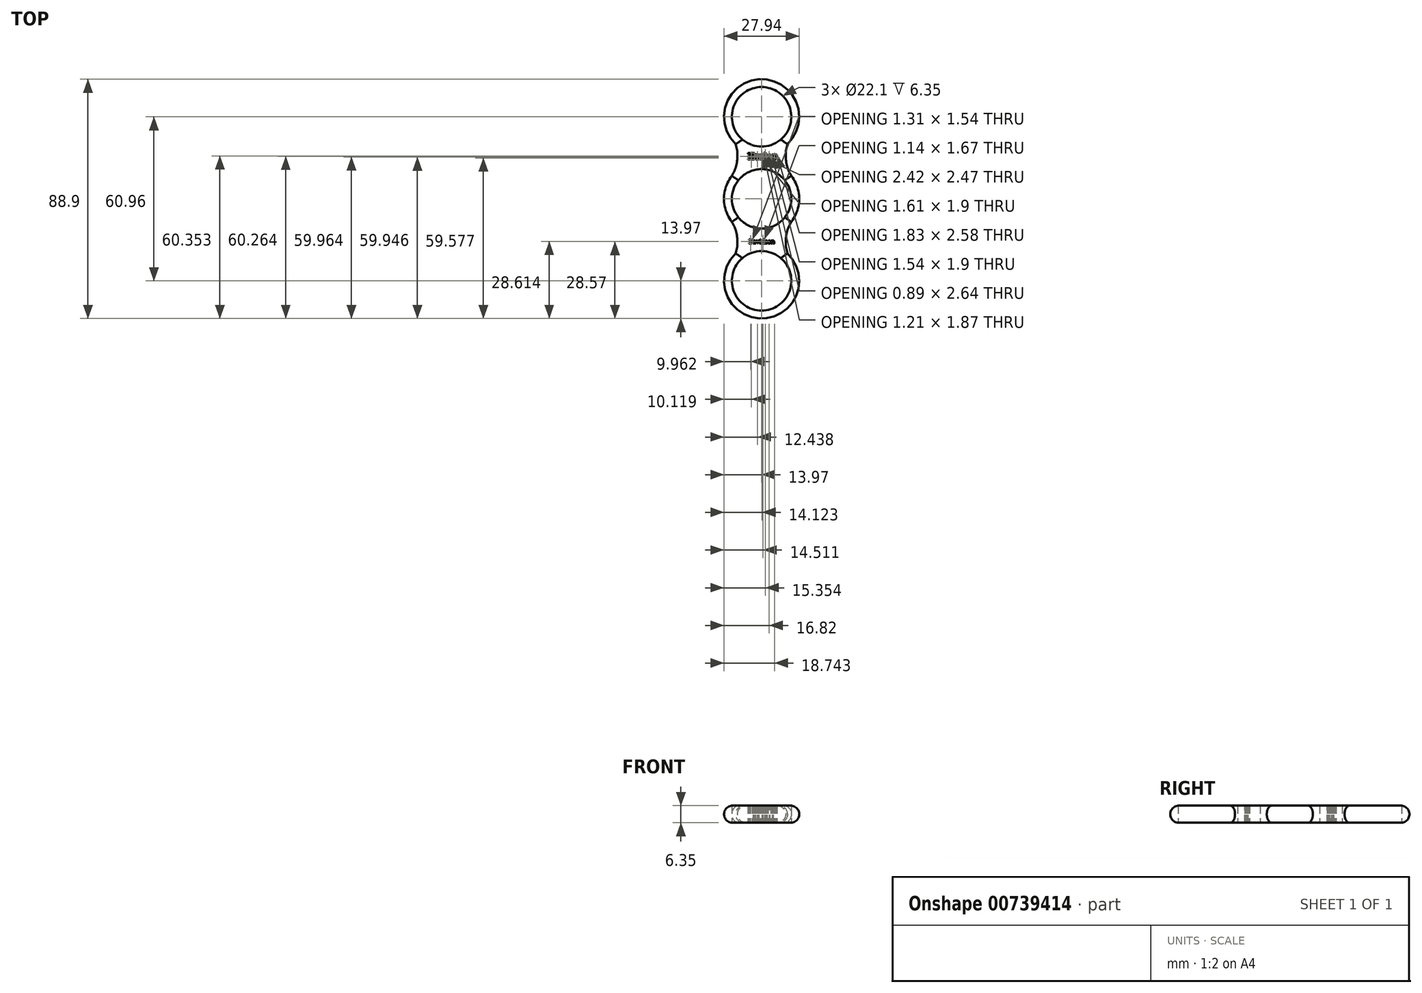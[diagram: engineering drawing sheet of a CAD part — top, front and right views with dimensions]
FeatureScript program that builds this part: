
annotation { "Feature Type Name" : "Feature", "Feature Type Description" : "" }
export const myFeature = defineFeature(function(context is Context, id is Id, definition is map)
    precondition{}
    {
        {
            var Q0;
            Q0=qCreatedBy(makeId("Top.planeOp"),FACE);
            var sketch = newSketch(context, id + "F0", { "sketchPlane" : qUnion([Q0])});
            skCircle(sketch, "E0", {"center": v(0, 0) * mm, "radius": 11.05 * mm});
            skArc(sketch, "E1", {"start": v(-11.04, 8.56) * mm, "mid": v(-13.97, 0) * mm, "end": v(-11.04, -8.56) * mm});
            skLineSegment(sketch, "E2", {"start": v(0, 0) * mm, "end": v(0, 30.48) * mm});
            skCircle(sketch, "E3", {"center": v(0, 30.48) * mm, "radius": 11.05 * mm});
            skArc(sketch, "E4", {"start": v(9.62, 20.35) * mm, "mid": v(0, 44.45) * mm, "end": v(-9.62, 20.35) * mm});
            skArc(sketch, "E5.MirrorC", {"start": v(9.62, -20.35) * mm, "mid": v(0, -44.45) * mm, "end": v(-9.62, -20.35) * mm});
            skCircle(sketch, "E6.MirrorC", {"center": v(0, -30.48) * mm, "radius": 11.05 * mm});
            skArc(sketch, "E7", {"start": v(-11.97, 7.2) * mm, "mid": v(-9, 17.08) * mm, "end": v(-13.37, 26.42) * mm});
            skArc(sketch, "E8.MirrorCS", {"start": v(11.97, 7.2) * mm, "mid": v(9, 17.08) * mm, "end": v(13.37, 26.42) * mm});
            skArc(sketch, "E9.MirrorCS", {"start": v(11.97, -7.2) * mm, "mid": v(9, -17.08) * mm, "end": v(13.37, -26.42) * mm});
            skArc(sketch, "E10.MirrorCS", {"start": v(-11.97, -7.2) * mm, "mid": v(-9, -17.08) * mm, "end": v(-13.37, -26.42) * mm});
            skArc(sketch, "E11.trimOffspring", {"start": v(11.04, -8.56) * mm, "mid": v(13.97, 0) * mm, "end": v(11.04, 8.56) * mm});
            skText(sketch, "E12", { "text": "Harley", "fontName": "RobotoSlab-Regular.ttf"});
            skPoint(sketch, "E12.firstSnap0", {"position": v(-9, 17.08) * mm});
            skText(sketch, "E13", { "text": "Davidson", "fontName": "RobotoSlab-Regular.ttf"});
            const initialGuessF0  = {"E12": [-0.00518, 0.01458, 1, 0, 0.0025], "E13": [-0.00474, -0.01665, 1, 0, 0.00156]};
            skSetInitialGuess(sketch, initialGuessF0);
            skSolve(sketch);
        }
        {
            var Q0;
            Q0 = qSketchRegion(id + "F0", true);
            extrude(context, id + "F1", {"entities" : qUnion([Q0]), "depth" : 6.35 * mm, "offsetDistance" : 25.4 * mm});
        }
        {
            var Q0;
            Q0=makeQuery(id+"F1.opExtrude","CAP_EDGE",EDGE,{"disambiguationData":[OSD([sQuery(id+"F0.wireOp",EDGE,"E4")])],"isStart":false});
            var Q1;
            Q1=makeQuery(id+"F1.opExtrude","CAP_EDGE",EDGE,{"disambiguationData":[OSD([sQuery(id+"F0.wireOp",EDGE,"E1")])],"isStart":false});
            var Q2;
            Q2=makeQuery(id+"F1.opExtrude","CAP_EDGE",EDGE,{"disambiguationData":[OSD([sQuery(id+"F0.wireOp",EDGE,"E7")])],"isStart":false});
            var Q3;
            Q3=makeQuery(id+"F1.opExtrude","CAP_EDGE",EDGE,{"disambiguationData":[OSD([sQuery(id+"F0.wireOp",EDGE,"E8.MirrorCS")])],"isStart":false});
            var Q4;
            Q4=makeQuery(id+"F1.opExtrude","CAP_EDGE",EDGE,{"disambiguationData":[OSD([sQuery(id+"F0.wireOp",EDGE,"E10.MirrorCS")])],"isStart":false});
            var Q5;
            Q5=makeQuery(id+"F1.opExtrude","CAP_EDGE",EDGE,{"disambiguationData":[OSD([sQuery(id+"F0.wireOp",EDGE,"E9.MirrorCS")])],"isStart":false});
            var Q6;
            Q6=makeQuery(id+"F1.opExtrude","CAP_EDGE",EDGE,{"disambiguationData":[OSD([sQuery(id+"F0.wireOp",EDGE,"E11.trimOffspring")])],"isStart":false});
            var Q7;
            Q7=makeQuery(id+"F1.opExtrude","CAP_EDGE",EDGE,{"disambiguationData":[OSD([sQuery(id+"F0.wireOp",EDGE,"E5.MirrorC")])],"isStart":false});
            var Q8;
            Q8=makeQuery(id+"F1.opExtrude","CAP_EDGE",EDGE,{"disambiguationData":[OSD([sQuery(id+"F0.wireOp",EDGE,"E5.MirrorC")])],"isStart":true});
            var Q9;
            Q9=makeQuery(id+"F1.opExtrude","CAP_EDGE",EDGE,{"disambiguationData":[OSD([sQuery(id+"F0.wireOp",EDGE,"E9.MirrorCS")])],"isStart":true});
            var Q10;
            Q10=makeQuery(id+"F1.opExtrude","CAP_EDGE",EDGE,{"disambiguationData":[OSD([sQuery(id+"F0.wireOp",EDGE,"E10.MirrorCS")])],"isStart":true});
            var Q11;
            Q11=makeQuery(id+"F1.opExtrude","CAP_EDGE",EDGE,{"disambiguationData":[OSD([sQuery(id+"F0.wireOp",EDGE,"E1")])],"isStart":true});
            var Q12;
            Q12=makeQuery(id+"F1.opExtrude","CAP_EDGE",EDGE,{"disambiguationData":[OSD([sQuery(id+"F0.wireOp",EDGE,"E11.trimOffspring")])],"isStart":true});
            var Q13;
            Q13=makeQuery(id+"F1.opExtrude","CAP_EDGE",EDGE,{"disambiguationData":[OSD([sQuery(id+"F0.wireOp",EDGE,"E7")])],"isStart":true});
            var Q14;
            Q14=makeQuery(id+"F1.opExtrude","CAP_EDGE",EDGE,{"disambiguationData":[OSD([sQuery(id+"F0.wireOp",EDGE,"E8.MirrorCS")])],"isStart":true});
            var Q15;
            Q15=makeQuery(id+"F1.opExtrude","CAP_EDGE",EDGE,{"disambiguationData":[OSD([sQuery(id+"F0.wireOp",EDGE,"E4")])],"isStart":true});
            fillet(context, id + "F2", {"entities" : qUnion([Q0, Q1, Q2, Q3, Q4, Q5, Q6, Q7, Q8, Q9, Q10, Q11, Q12, Q13, Q14, Q15]), "radius" : 3.17 * mm, "tangentPropagation" : true, "allowEdgeOverflow" : false});
        }
    });
